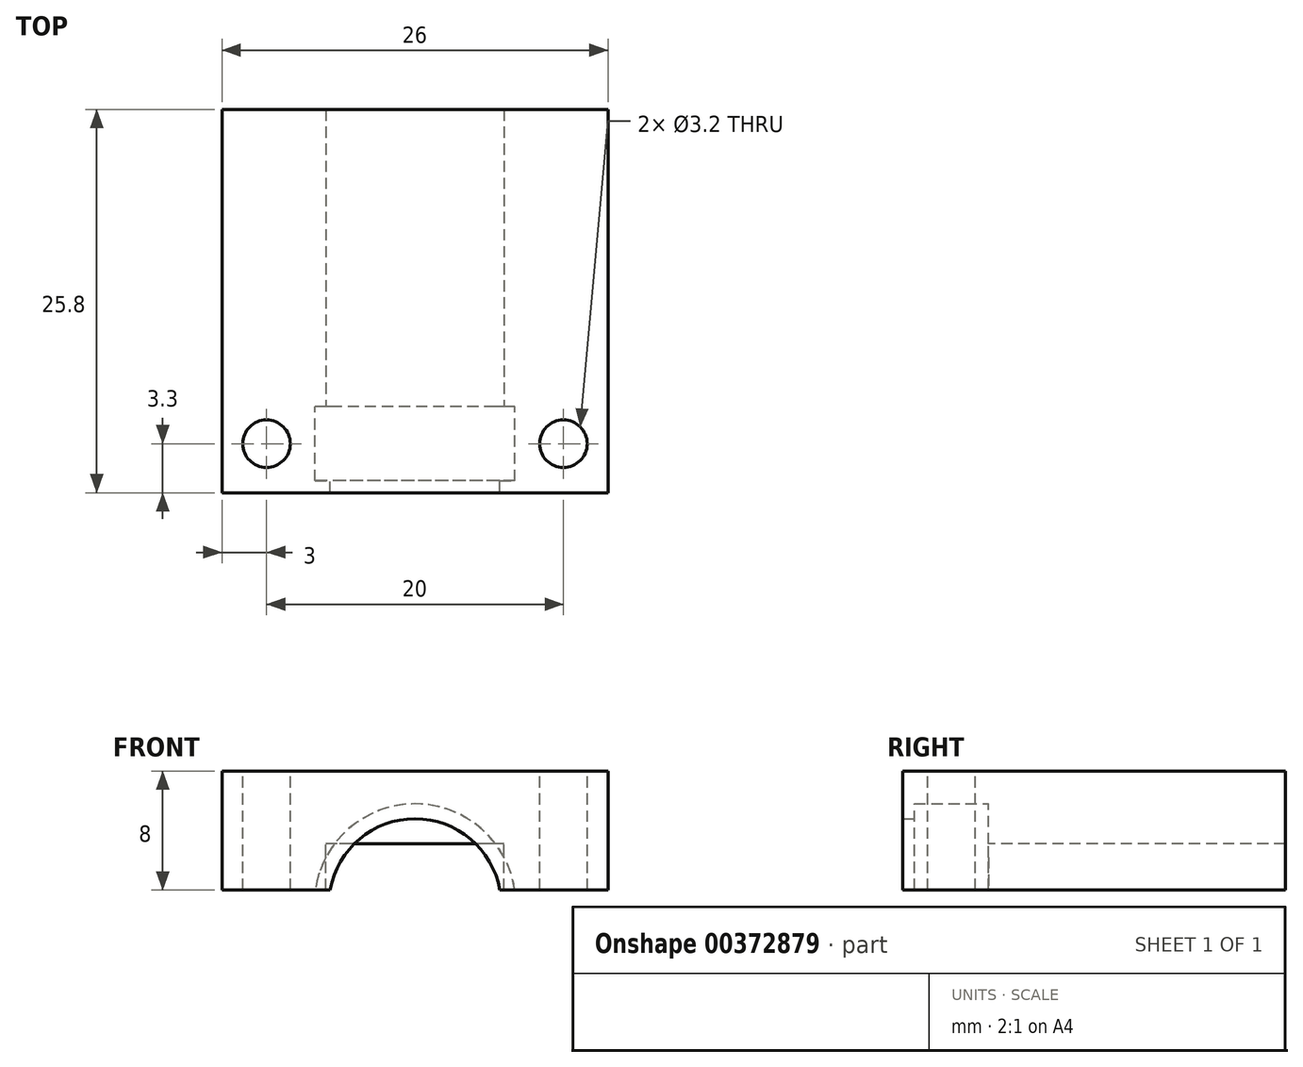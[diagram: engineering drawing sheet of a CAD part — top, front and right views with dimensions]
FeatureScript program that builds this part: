
annotation { "Feature Type Name" : "Feature", "Feature Type Description" : "" }
export const myFeature = defineFeature(function(context is Context, id is Id, definition is map)
    precondition{}
    {
        {
            var Q0;
            Q0=qCreatedBy(makeId("Front.planeOp"),FACE);
            var sketch = newSketch(context, id + "F0", { "sketchPlane" : qUnion([Q0])});
            skLineSegment(sketch, "E0.bottom", {"start": v(-13, 4) * mm, "end": v(13, 4) * mm});
            skLineSegment(sketch, "E0.top", {"start": v(-13, -4) * mm, "end": v(-6.73, -4) * mm});
            skLineSegment(sketch, "E0.left", {"start": v(-13, 4) * mm, "end": v(-13, -4) * mm});
            skLineSegment(sketch, "E0.right", {"start": v(13, 4) * mm, "end": v(13, -4) * mm});
            skArc(sketch, "E1", {"start": v(6.73, -4) * mm, "mid": v(0, 1.8) * mm, "end": v(-6.73, -4) * mm});
            skLineSegment(sketch, "E2", {"start": v(-13, 4) * mm, "end": v(13, -4) * mm, "construction": true});
            skLineSegment(sketch, "E3.trimOffspring", {"start": v(6.73, -4) * mm, "end": v(13, -4) * mm});
            skLineSegment(sketch, "E4", {"start": v(0, 0) * mm, "end": v(0, -5) * mm});
            skSolve(sketch);
        }
        {
            var Q0;
            Q0=qSketchRegion(id+"F0",true);
            extrude(context, id + "F1", {"entities" : qUnion([Q0]), "endBound" : BoundingType.SYMMETRIC, "depth" : 5 * mm, "offsetDistance" : 25 * mm});
        }
        {
            var Q0;
            Q0=qCreatedBy(makeId("Top.planeOp"),FACE);
            var sketch = newSketch(context, id + "F2", { "sketchPlane" : qUnion([Q0])});
            skLineSegment(sketch, "E5", {"start": v(-10, 0) * mm, "end": v(10, 0) * mm, "construction": true});
            skCircle(sketch, "E6", {"center": v(10, 0) * mm, "radius": 1.6 * mm});
            skCircle(sketch, "E7", {"center": v(-10, 0) * mm, "radius": 1.6 * mm});
            skSolve(sketch);
        }
        {
            var Q0;
            Q0=qSketchRegion(id+"F2",true);
            extrude(context, id + "F3", {"entities" : qUnion([Q0]), "operationType" : NewBodyOperationType.REMOVE, "endBound" : BoundingType.SYMMETRIC, "oppositeDirection" : true, "depth" : 25 * mm, "offsetDistance" : 25 * mm});
        }
        {
            var Q0;
            Q0=makeQuery(id+"F1.opExtrude","CAP_FACE",FACE,{"disambiguationData":[OSD([sQuery(id+"F0.wireOp",EDGE,"E0.bottom"),sQuery(id+"F0.wireOp",EDGE,"E0.top"),sQuery(id+"F0.wireOp",EDGE,"E0.left"),sQuery(id+"F0.wireOp",EDGE,"E0.right"),sQuery(id+"F0.wireOp",EDGE,"E1"),sQuery(id+"F0.wireOp",EDGE,"E3.trimOffspring")])],"isStart":true});
            cPlane(context, id + "F4", {"entities" : qUnion([Q0]), "cplaneType" : CPlaneType.OFFSET, "offset" : 0 * mm, "width" : 150 * mm, "height" : 150 * mm});
        }
        {
            var Q0;
            Q0=qCreatedBy(id+"F4.planeOp",FACE);
            var sketch = newSketch(context, id + "F5", { "sketchPlane" : qUnion([Q0])});
            skLineSegment(sketch, "E8.bottom", {"start": v(-13, 4) * mm, "end": v(13, 4) * mm});
            skLineSegment(sketch, "E8.top", {"start": v(-13, -4) * mm, "end": v(-6, -4) * mm});
            skLineSegment(sketch, "E8.left", {"start": v(-13, 4) * mm, "end": v(-13, -4) * mm});
            skLineSegment(sketch, "E8.right", {"start": v(13, 4) * mm, "end": v(13, -4) * mm});
            skLineSegment(sketch, "E9.top", {"start": v(-6, -0.9) * mm, "end": v(6, -0.9) * mm});
            skLineSegment(sketch, "E9.left", {"start": v(-6, -4) * mm, "end": v(-6, -0.9) * mm});
            skLineSegment(sketch, "E9.right", {"start": v(6, -4) * mm, "end": v(6, -0.9) * mm});
            skLineSegment(sketch, "E10.trimOffspring", {"start": v(6, -4) * mm, "end": v(13, -4) * mm});
            skSolve(sketch);
        }
        {
            var Q0;
            Q0 = qSketchRegion(id + "F5", true);
            extrude(context, id + "F6", {"entities" : qUnion([Q0]), "operationType" : NewBodyOperationType.ADD, "depth" : 20 * mm, "offsetDistance" : 25 * mm});
        }
        {
            var Q0;
            Q0=makeQuery(id+"F1.opExtrude","CAP_FACE",FACE,{"disambiguationData":[OSD([sQuery(id+"F0.wireOp",EDGE,"E0.bottom"),sQuery(id+"F0.wireOp",EDGE,"E0.top"),sQuery(id+"F0.wireOp",EDGE,"E0.left"),sQuery(id+"F0.wireOp",EDGE,"E0.right"),sQuery(id+"F0.wireOp",EDGE,"E1"),sQuery(id+"F0.wireOp",EDGE,"E3.trimOffspring")])],"isStart":false});
            cPlane(context, id + "F7", {"entities" : qUnion([Q0]), "cplaneType" : CPlaneType.OFFSET, "offset" : 0 * mm, "width" : 150 * mm, "height" : 150 * mm});
        }
        {
            var Q0;
            Q0=qCreatedBy(id+"F7.planeOp",FACE);
            var sketch = newSketch(context, id + "F8", { "sketchPlane" : qUnion([Q0])});
            skLineSegment(sketch, "E11.bottom", {"start": v(-13, 4) * mm, "end": v(13, 4) * mm});
            skLineSegment(sketch, "E11.top", {"start": v(-13, -4) * mm, "end": v(-5.71, -4) * mm});
            skLineSegment(sketch, "E11.left", {"start": v(-13, 4) * mm, "end": v(-13, -4) * mm});
            skLineSegment(sketch, "E11.right", {"start": v(13, 4) * mm, "end": v(13, -4) * mm});
            skArc(sketch, "E12", {"start": v(5.71, -4) * mm, "mid": v(0, 0.8) * mm, "end": v(-5.71, -4) * mm});
            skLineSegment(sketch, "E13.trimOffspring", {"start": v(5.71, -4) * mm, "end": v(13, -4) * mm});
            skSolve(sketch);
        }
        {
            var Q0;
            Q0 = qSketchRegion(id + "F8", true);
            extrude(context, id + "F9", {"entities" : qUnion([Q0]), "operationType" : NewBodyOperationType.ADD, "depth" : 0.8 * mm, "offsetDistance" : 25 * mm});
        }
    });
